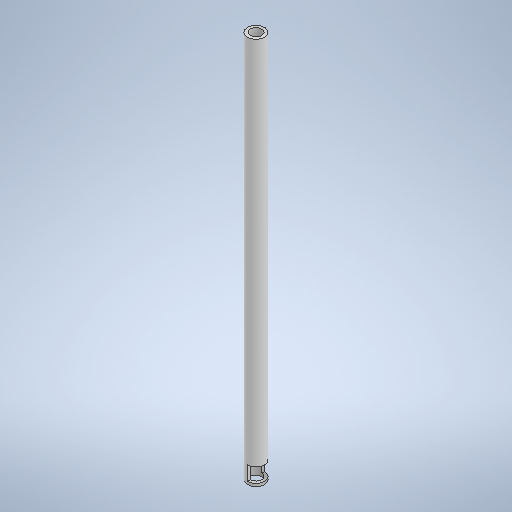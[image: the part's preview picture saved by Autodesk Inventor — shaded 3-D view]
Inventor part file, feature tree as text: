
AUTODESK INVENTOR PART (.ipt)
format: ipt  version: 2025 (Build 290162000, 162)  size: 275,456 bytes
history: native  units: mm
features: extrude x4, sketch x4, other x1
ambient origin geometry x8: Origin, YZ Plane, XZ Plane, XY Plane, X Axis, Y Axis, Z Axis, Center Point
bodies: Body1 (feature_tree)
feature tree (9):
  other  "Bryła1"
  extrude  "Wyciągnięcie proste1"  Depth=6.0mm
  sketch  "Szkic2"
  extrude  "Wyciągnięcie proste2"  Depth=4.0mm
  extrude  "Wyciągnięcie proste3"  Depth=135.0mm TaperAngle=0.0deg
  extrude  "Wyciągnięcie proste4"  Depth=6.0mm
  sketch  "Szkic1"
  sketch  "Szkic3"
  sketch  "Szkic4"
